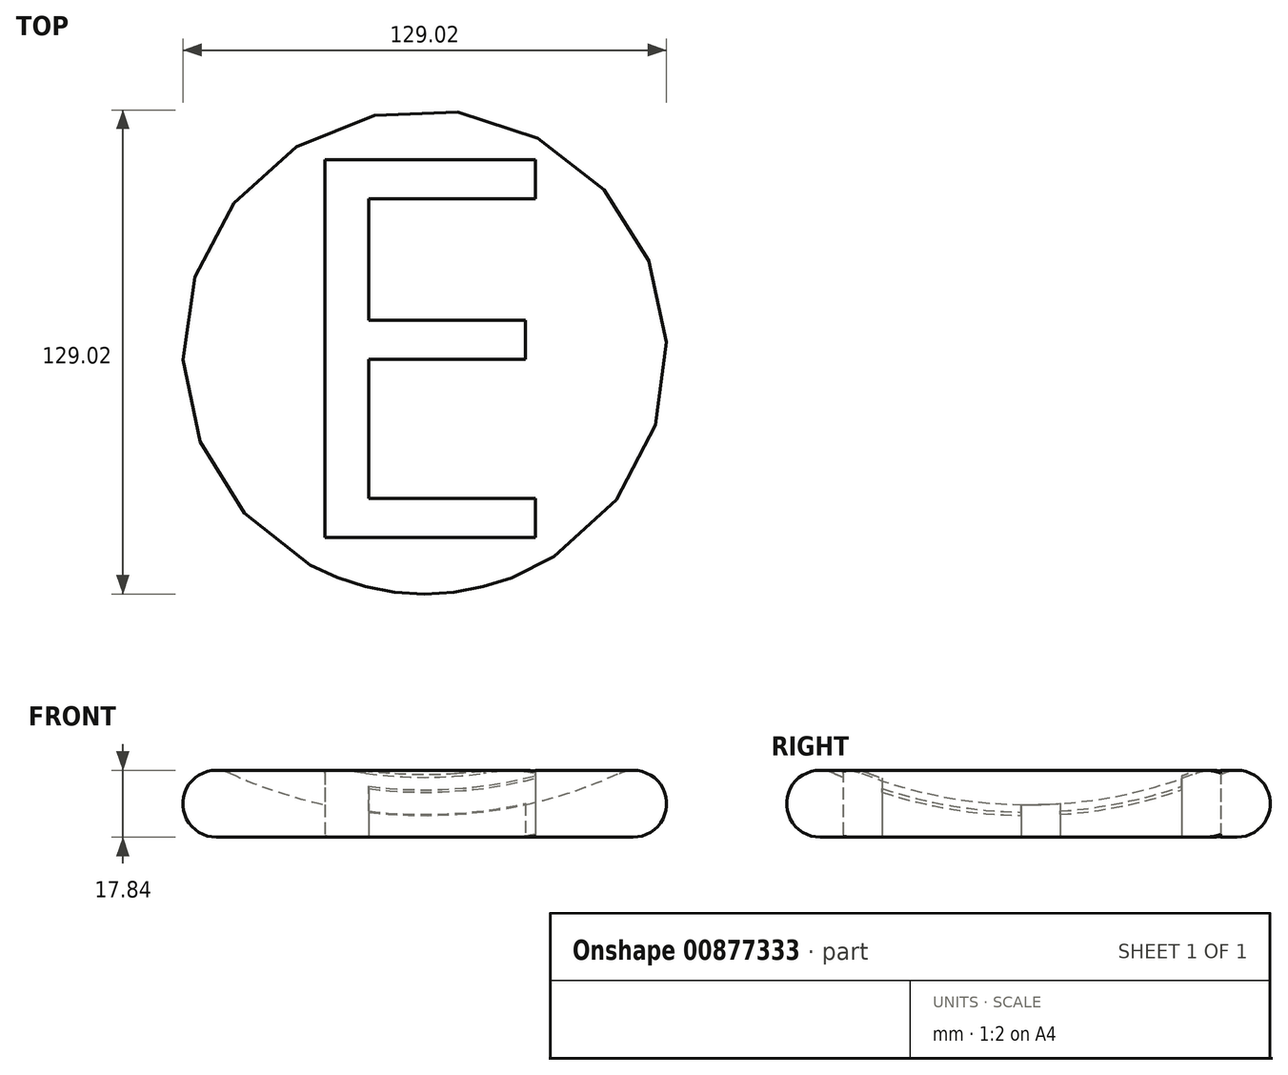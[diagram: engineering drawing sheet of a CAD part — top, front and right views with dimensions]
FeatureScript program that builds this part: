
annotation { "Feature Type Name" : "Feature", "Feature Type Description" : "" }
export const myFeature = defineFeature(function(context is Context, id is Id, definition is map)
    precondition{}
    {
        {
            var Q0;
            Q0=qCreatedBy(makeId("Front.planeOp"),FACE);
            var sketch = newSketch(context, id + "F0", { "sketchPlane" : qUnion([Q0])});
            skArc(sketch, "E0", {"start": v(-51.9, 17.03) * mm, "mid": v(-64.3, 10.8) * mm, "end": v(-55.6, 0) * mm});
            skArc(sketch, "E1", {"start": v(-51.9, 17.03) * mm, "mid": v(-26.55, 8.62) * mm, "end": v(0, 5.77) * mm});
            skLineSegment(sketch, "E2", {"start": v(0, 0) * mm, "end": v(0, 5.77) * mm});
            skLineSegment(sketch, "E3", {"start": v(0, 0) * mm, "end": v(-55.6, 0) * mm});
            skSolve(sketch);
        }
        {
            var Q0;
            Q0 = qSketchRegion(id + "F0", true);
            var Q1;
            Q1=sQuery(id+"F0.wireOp",EDGE,"E2");
            revolve(context, id + "F1", {"surfaceOperationType" : NewSurfaceOperationType.NEW, "entities" : qUnion([Q0]), "axis" : qUnion([Q1]), "revolveType" : RevolveType.FULL});
        }
        {
            var Q0;
            Q0=qCreatedBy(makeId("Top.planeOp"),FACE);
            var sketch = newSketch(context, id + "F2", { "sketchPlane" : qUnion([Q0])});
            skText(sketch, "E4", { "text": "E", "fontName": "OpenSans-Regular.ttf"});
            const initialGuessF2  = {"E4": [-0.04044, -0.04946, 1, 0, 0.1016]};
            skSetInitialGuess(sketch, initialGuessF2);
            skSolve(sketch);
        }
        {
            var Q0;
            Q0 = qSketchRegion(id + "F2", true);
            extrude(context, id + "F3", {"entities" : qUnion([Q0]), "operationType" : NewBodyOperationType.REMOVE, "depth" : 25.4 * mm, "offsetDistance" : 25.4 * mm});
        }
    });
